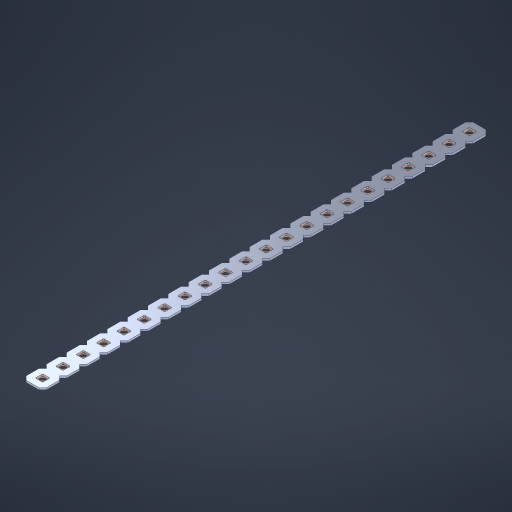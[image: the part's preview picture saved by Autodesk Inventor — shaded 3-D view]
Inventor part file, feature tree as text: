
AUTODESK INVENTOR PART (.ipt)
format: ipt  version: 2023 (Build 270158000, 158)  size: 542,208 bytes
history: native  units: in
note: dims shown in document units (in); Inventor stores cm internally (conversion verified against a paired STEP export)
features: other x23, extrude x21, sketch x2, pattern_linear x1
ambient origin geometry x8: Origin, YZ Plane, XZ Plane, XY Plane, X Axis, Y Axis, Z Axis, Center Point
bodies: Solid1 (feature_tree), Body (feature_tree)
feature tree (47):
  pattern_linear  "Rectangular Pattern1"  Spacing1=0.09in  [1 undecoded]
  sketch  "Sketch1"  dims[d1=0.5in]
  sketch  "Sketch2"  dims[d2=0.182in d3=0.09in d4=0.09in d5=0.09in d6=0.09in d7=0.09in d8=0.09in d9=0.09in d10=0.09in d11=0.02in d13=0.0in d14=0.172in d15=0.0625in d16=0.0in d19=0.5in d22=0.5in]
  other  "Srf1"
  other  "Srf126"
  other  "Srf127"
  other  "Srf128"
  other  "Srf129"
  other  "Srf130"
  other  "Srf131"
  other  "Srf250"
  other  "Srf251"
  other  "Srf252"
  other  "Srf253"
  other  "Srf254"
  other  "Srf255"
  other  "Srf256"
  other  "Srf257"
  other  "Srf258"
  other  "Srf259"
  other  "Srf260"
  other  "Srf261"
  other  "Srf262"
  other  "Srf263"
  other  "Srf264"
  other  "Circle"
  extrude  "ExtrusionSrf126"  Depth=0.09in
  extrude  "ExtrusionSrf127"  Depth=0.09in
  extrude  "ExtrusionSrf128"  Depth=0.09in
  extrude  "ExtrusionSrf129"  Depth=0.09in
  extrude  "ExtrusionSrf130"  Depth=0.09in
  extrude  "ExtrusionSrf131"  Depth=0.09in
  extrude  "ExtrusionSrf250"  Depth=0.09in
  extrude  "ExtrusionSrf251"  Depth=0.02in
  extrude  "ExtrusionSrf252"  TaperAngle=0.0deg  [1 undecoded]
  extrude  "ExtrusionSrf253"  Depth=0.5in
  extrude  "ExtrusionSrf254"  Depth=0.5in TaperAngle=0.0deg
  extrude  "ExtrusionSrf255"  Depth=0.5in
  extrude  "ExtrusionSrf256"  Depth=0.5in
  extrude  "ExtrusionSrf257"  [1 undecoded]
  extrude  "ExtrusionSrf258"  [1 undecoded]
  extrude  "ExtrusionSrf259"  [1 undecoded]
  extrude  "ExtrusionSrf260"  [1 undecoded]
  extrude  "ExtrusionSrf261"  [1 undecoded]
  extrude  "ExtrusionSrf262"  [1 undecoded]
  extrude  "ExtrusionSrf263"  [1 undecoded]
  extrude  "ExtrusionSrf264"  [1 undecoded]
note: 10 required parameter values undecoded (feature->parameter linkage not recoverable at this tier; creation-order binding heuristic only, values carry confidence <= 0.55)
